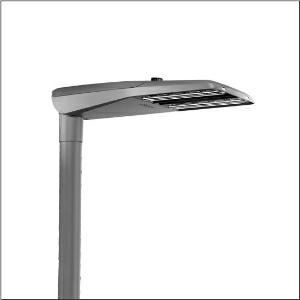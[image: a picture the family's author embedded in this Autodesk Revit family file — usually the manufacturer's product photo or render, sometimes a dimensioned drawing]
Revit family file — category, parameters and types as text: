
# Revit family: streetlight_sl_11_iq_midi___st1_2a_5xc3a51u08me_6b2b
name_source: partatom
category: Lighting Fixtures
units: mm (PartAtom-declared; Revit-internal decimal feet)

## family parameters
Cut with Voids When Loaded = No
Host = Face
Light Source = No
Part Type = Normal
Room Calculation Point = No
Round Connector Dimension = Use Diameter
Shared = No

## types (1)
- --- (1 x LED, 18110 lm, 122.7 W, 3000K)
    Apparent Load = 123 VA
    CIE Flux Codes = 32 70 96 100 100
    Color Rendering = 70
    Color Temperature = 3000K
    Default Elevation = 1800 mm
    Description = Streetlight SL 11 iQ midi, mast luminaire, primary light control with 3 zone facetted reflector, of plastic, silver coated, highly specular, primary optical cover: cover, of PMMA, transparent, light distribution: ST1.2a, light emission: direct distribution, primary light characteristic: asymmetric, installation type: post-top, side-entry, LED, High Power LED, rated luminous flux: 18.110lm, luminous efficacy: 148lm/W, light colour: 730, colour temperature: 3000K, control: presetting dimming logarithmic, Street-Remote, Auto-Match, Temp-Guard, Lumen-Switch, Night-Set, Smart-Wire, Light-Fading, Desk-Remote (wireless, voltage-free reading and setting of iQ features in the workshop via application-optimized NFC function/RFID function), optimised constant luminous flux control (CLO 2.0), with cable H07RN-F 5x 1.5mm², mains connection: 230..240V, AC, 50/60Hz, connection cable pre-assembled, cable length: 12,5m, start of lifetime: 123W, end of service life: 130W, reduction: 56W, luminaire housing, of diecast aluminium, powder-coated, Siteco® metallic grey (DB 702S), please order mast flange separately, inclination adjustable without tools: 0°, 5°, 10°, 15° (post-top) | 0°, -5°, -10°, -15° (side-entry), sealing non-destructively replaceable, multi-level sealing system, length: 780mm, width: 376mm, height: 118mm, mast flange for spigot size: 42mm (side-entry): 5XC10008XM4, 60/48mm (side-entry/post-top): 5XC10108XM2, 76/60mm (side-entry/post-top): 5XC10108XM1, equipment: Power, Smart Interface below, protection rating (complete): IP66, insulation class (complete): insulation class II (safety insulation), certification: CE, ENEC, VDE, UKCA, impact resistance: IK09, permissible operating ambient temperature for outdoor applications: -25..+50°C, standard-compliant lighting for roads and squares, Environmental Product Declaration (EPD) tested and certified by an independent institute, packaging unit: 1 piece

Light Distribution: ST1.2a
    Height = 118 mm
    Lamp = 1 x LED
    Lamp Light Flux = 18110 lm
    Lamp Power = 122.7 W
    Lamp count = 1
    Length = 780 mm
    Luminous efficacy = 148 lm/W
    Manufacturer = Siteco
    ModVariant = No
    Model = 5XC3A51U08ME
    Number of Poles = 1
    OnlyDefault = Yes
    Power Factor = 1
    Product Name = Streetlight SL 11 iQ midi | ST1.2a
    Product group = mast luminaire | pylon top
    ProductGroupID = 6100
    Protection Class = Protection class II
    Protection Degree = IP 66
    RLX_Detail_Level = 1
    RLX_Emergency_Light_Flux = 0 lm
    RLX_Emergency_Type = 0
    RLX_Emergency_Type_DB = No
    RlxData = <blob elided: 69809 chars, md5=754a60f8>
    Socket = socket
    Standby Power = 0 W
    System Light Flux = 18111 lm
    System Power = 123 W
    Type Comments = factory setting: luminous flux: 100 % | dim-lin: 254 | 553 mA
    Type Image = l_1005968.jpg
    URL = http://relux.com
    VarID = @adj_082605
    Voltage = 0 V
    Weight = 0.00 kg
    Width = 376 mm

## geometry (parser evidence)
native form markers: Blend x4, Sweep x8
no freeform markers — native parametric forms only
